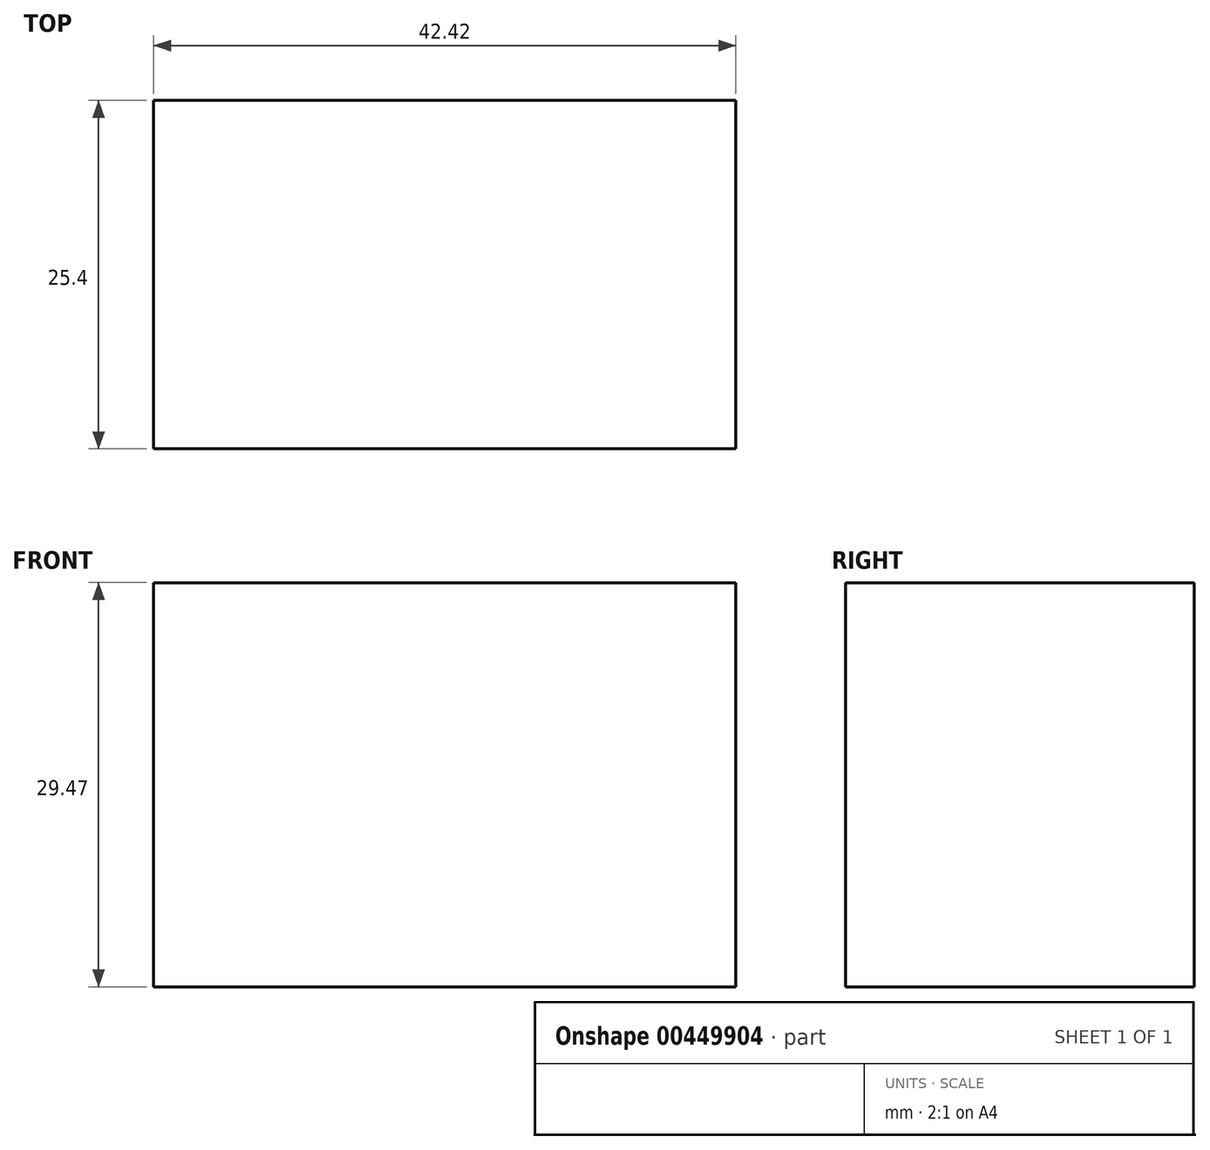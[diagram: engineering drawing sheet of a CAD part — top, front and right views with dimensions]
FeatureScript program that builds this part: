
annotation { "Feature Type Name" : "Feature", "Feature Type Description" : "" }
export const myFeature = defineFeature(function(context is Context, id is Id, definition is map)
    precondition{}
    {
        {
            var Q0;
            Q0=qCreatedBy(makeId("Front.planeOp"),FACE);
            var sketch = newSketch(context, id + "F0", { "sketchPlane" : qUnion([Q0])});
            skLineSegment(sketch, "E0.bottom", {"start": v(-16.26, 13.72) * mm, "end": v(26.16, 13.72) * mm});
            skLineSegment(sketch, "E0.top", {"start": v(-16.26, -15.75) * mm, "end": v(26.16, -15.75) * mm});
            skLineSegment(sketch, "E0.left", {"start": v(-16.26, 13.72) * mm, "end": v(-16.26, -15.75) * mm});
            skLineSegment(sketch, "E0.right", {"start": v(26.16, 13.72) * mm, "end": v(26.16, -15.75) * mm});
            skSolve(sketch);
        }
        {
            var Q0;
            Q0 = qSketchRegion(id + "F0", true);
            extrude(context, id + "F1", {"entities" : qUnion([Q0]), "depth" : 25.4 * mm});
        }
    });
